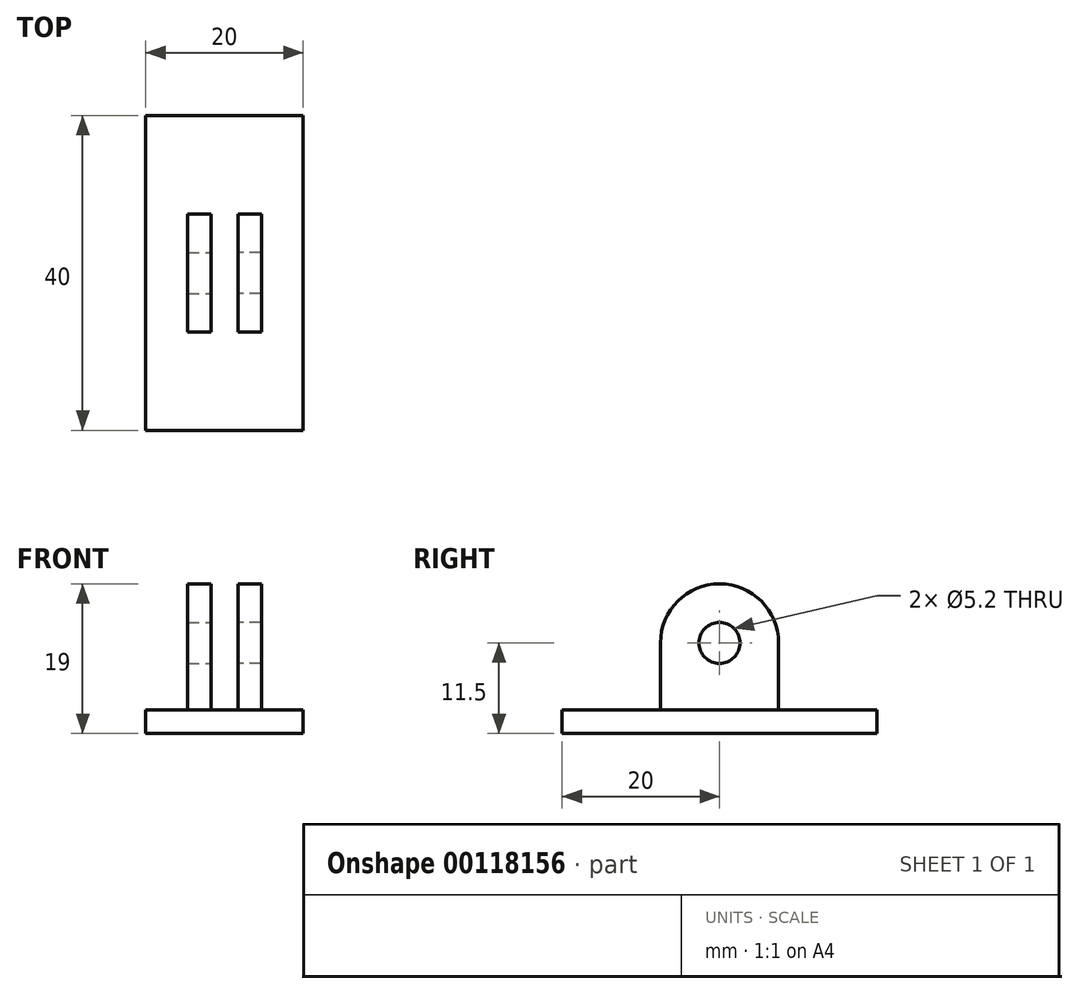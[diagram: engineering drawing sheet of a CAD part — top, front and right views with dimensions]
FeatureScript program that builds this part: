
annotation { "Feature Type Name" : "Feature", "Feature Type Description" : "" }
export const myFeature = defineFeature(function(context is Context, id is Id, definition is map)
    precondition{}
    {
        {
            var Q0;
            Q0=qCreatedBy(makeId("Right.planeOp"),FACE);
            cPlane(context, id + "F0", {"entities" : qUnion([Q0]), "cplaneType" : CPlaneType.OFFSET, "offset" : (3.4 / 2) * mm, "width" : 150 * mm, "height" : 150 * mm});
        }
        {
            var Q0;
            Q0=qCreatedBy(id+"F0.planeOp",FACE);
            var sketch = newSketch(context, id + "F1", { "sketchPlane" : qUnion([Q0])});
            skLineSegment(sketch, "E0", {"start": v(0, 0) * mm, "end": v(0, 8.5) * mm, "construction": true});
            skCircle(sketch, "E1", {"center": v(0, 8.5) * mm, "radius": 2.6 * mm});
            skArc(sketch, "E2", {"start": v(7.5, 8.5) * mm, "mid": v(0, 16) * mm, "end": v(-7.5, 8.5) * mm});
            skLineSegment(sketch, "E3", {"start": v(0, 8.5) * mm, "end": v(-7.5, 8.5) * mm, "construction": true});
            skLineSegment(sketch, "E4", {"start": v(-7.5, 8.5) * mm, "end": v(-7.5, 0) * mm});
            skLineSegment(sketch, "E5.MirrorCS", {"start": v(7.5, 8.5) * mm, "end": v(7.5, 0) * mm});
            skLineSegment(sketch, "E6", {"start": v(-7.5, 0) * mm, "end": v(7.5, 0) * mm});
            skSolve(sketch);
        }
        {
            var Q0;
            Q0 = qSketchRegion(id + "F1", true);
            extrude(context, id + "F2", {"entities" : qUnion([Q0]), "depth" : 3 * mm});
        }
        {
            var Q0;
            Q0=makeQuery(id+"F2.opExtrude","SWEPT_BODY",BODY,{"disambiguationData":[OSD([sQuery(id+"F1.wireOp",EDGE,"E1"),sQuery(id+"F1.wireOp",EDGE,"E2"),sQuery(id+"F1.wireOp",EDGE,"E4"),sQuery(id+"F1.wireOp",EDGE,"E5.MirrorCS"),sQuery(id+"F1.wireOp",EDGE,"E6")])]});
            var Q1;
            Q1=makeQuery(id+"F2.opExtrude","CAP_FACE",FACE,{"disambiguationData":[OSD([sQuery(id+"F1.wireOp",EDGE,"E1"),sQuery(id+"F1.wireOp",EDGE,"E2"),sQuery(id+"F1.wireOp",EDGE,"E4"),sQuery(id+"F1.wireOp",EDGE,"E5.MirrorCS"),sQuery(id+"F1.wireOp",EDGE,"E6")])],"isStart":true});
            var Q2;
            Q2=qCreatedBy(makeId("Right.planeOp"),FACE);
            mirror(context, id + "F3", {"entities" : qUnion([Q0]), "faces" : qUnion([Q1]), "mirrorPlane" : qUnion([Q2])});
        }
        {
            var Q0;
            Q0=qCreatedBy(makeId("Top.planeOp"),FACE);
            var sketch = newSketch(context, id + "F4", { "sketchPlane" : qUnion([Q0])});
            skLineSegment(sketch, "E7.bottom", {"start": v(10, -20) * mm, "end": v(-10, -20) * mm});
            skLineSegment(sketch, "E7.top", {"start": v(10, 20) * mm, "end": v(-10, 20) * mm});
            skLineSegment(sketch, "E7.left", {"start": v(10, -20) * mm, "end": v(10, 20) * mm});
            skLineSegment(sketch, "E7.right", {"start": v(-10, -20) * mm, "end": v(-10, 20) * mm});
            skPoint(sketch, "E7.middle", {"position": v(0, 0) * mm});
            skSolve(sketch);
        }
        {
            var Q0;
            Q0 = qSketchRegion(id + "F4", true);
            extrude(context, id + "F5", {"entities" : qUnion([Q0]), "oppositeDirection" : true, "depth" : 3 * mm});
        }
    });
